# Revit family: CFP - CVP_ISD 1093 Generic
name_source: partatom
category: Windows
revit_build: Autodesk Revit Architecture 2014 (Build: 20130308_1515(x64)
units: mm (PartAtom-declared; Revit-internal decimal feet)

## types (8) — shared parameters
AcousticRating = 37
AllowedRoofSlope = 0°-15°
Analytic Construction = <None>
Assembly Code = B3020110
Coarse Profile = Yes
CoatingInternal = White PVC
Colour = Aluminium profiles / 5 mm toughened glass pane
Count = 1
EmergencyExit = No
Features = Ventilation flat roof window
Finish = PVC Color NCS S 0502-Y
FireRating = E
Function = Flat roof window
Glazing = 5mm Toughened Glass
IsExternal = Yes
LightTransmittance = 0.72
Material = Aluminium profiles / 5 mm toughened glass pane
MaterialsExternal = Aluminium profiles / 5 mm toughened glass pane
Model = Flat roof window
OffsetFromRoof = 400 mm  [stored 1.31234 ft]
Opening Lines Offset = 262.072 mm  [stored 0.859816 ft]
ReactionToFireClass = E
SmokeStop = No
SoundInsulation db = 37
ThermalResistance(R) = 0.0000 (m²·K)/W
UltravioletTransmittance = 0.05
WarrantyYears = 10
ZCEVisible = No
g-value = 0.51
zero-valued in all types: DefaultModel3DSlope, PlacementHeight, ThermalBridge(Installation) W/mK, ZCEHeight

## per-type parameters (varying)
| type | DomeProfileLength | Half Height | HalfHeight | HalfWidth | Height | Height Dome | Height External Profile | Height Outer Glass | Height Top Unit | NominalHeight | NominalWidth | PerimeterWindow m | Thickness Glass | Width | Width External Profile | Width Outer Glass | Width Silk Screen Print | WidthDome | WithinStandardSizes |
| CVP / CFP size 600x600 (060060) | 387.5 mm  [stored 1.27133 ft] | 300 mm  [stored 0.984252 ft] | 387.5 mm  [stored 1.27133 ft] | 387.5 mm  [stored 1.27133 ft] | 780 mm  [stored 2.55906 ft] | 600 mm  [stored 1.9685 ft] | 756 mm  [stored 2.48031 ft] | 746 mm  [stored 2.44751 ft] | 139 mm  [stored 0.456037 ft] | 780 | 780 | 2.4 | 6 mm  [stored 0.019685 ft] | 780 mm  [stored 2.55906 ft] | 756 mm  [stored 2.48031 ft] | 746 mm  [stored 2.44751 ft] | 650 mm  [stored 2.13255 ft] | 600 mm  [stored 1.9685 ft] | Yes |
| CVP / CFP size 1000x1500 (100150) | 587.5 mm | 750 mm  [stored 2.46063 ft] | 837.5 mm  [stored 2.7477 ft] | 587.5 mm | 1680 mm | 1500 mm | 1656 mm | 1646 mm | 190 mm | 1180 | 1680 | 5 | 6 mm  [stored 0.019685 ft] | 1180 mm | 1156 mm  [stored 3.79265 ft] | 1146 mm  [stored 3.75984 ft] | 1050 mm | 1000 mm  [stored 3.28084 ft] | No |
| CVP / CFP size 900x900 (090090) | 537.5 mm | 450 mm  [stored 1.47638 ft] | 537.5 mm | 537.5 mm | 1080 mm  [stored 3.54331 ft] | 900 mm  [stored 2.95276 ft] | 1056 mm  [stored 3.46457 ft] | 1046 mm  [stored 3.43176 ft] | 151 mm  [stored 0.495407 ft] | 1080 | 1080 | 3.6 | 5 mm  [stored 0.0164042 ft] | 1080 mm  [stored 3.54331 ft] | 1056 mm  [stored 3.46457 ft] | 1046 mm  [stored 3.43176 ft] | 950 mm  [stored 3.1168 ft] | 900 mm  [stored 2.95276 ft] | Yes |
| CVP / CFP size 800x800 (080080) | 487.5 mm  [stored 1.59941 ft] | 400 mm  [stored 1.31234 ft] | 487.5 mm  [stored 1.59941 ft] | 487.5 mm  [stored 1.59941 ft] | 980 mm  [stored 3.21522 ft] | 800 mm  [stored 2.62467 ft] | 956 mm  [stored 3.13648 ft] | 946 mm  [stored 3.10367 ft] | 147 mm  [stored 0.482283 ft] | 980 | 980 | 3.2 | 5 mm  [stored 0.0164042 ft] | 980 mm  [stored 3.21522 ft] | 956 mm  [stored 3.13648 ft] | 946 mm  [stored 3.10367 ft] | 850 mm  [stored 2.78871 ft] | 800 mm  [stored 2.62467 ft] | Yes |
| CVP / CFP size 900x1200 (090120) | 537.5 mm | 600 mm  [stored 1.9685 ft] | 687.5 mm  [stored 2.25558 ft] | 537.5 mm | 1380 mm | 1200 mm | 1356 mm | 1346 mm | 169 mm  [stored 0.554462 ft] | 1080 | 1380 | 4.2 | 6 mm  [stored 0.019685 ft] | 1080 mm  [stored 3.54331 ft] | 1056 mm  [stored 3.46457 ft] | 1046 mm  [stored 3.43176 ft] | 950 mm  [stored 3.1168 ft] | 900 mm  [stored 2.95276 ft] | No |
| CVP / CFP size 600x900 (060090) | 387.5 mm  [stored 1.27133 ft] | 450 mm  [stored 1.47638 ft] | 537.5 mm | 387.5 mm  [stored 1.27133 ft] | 1080 mm  [stored 3.54331 ft] | 900 mm  [stored 2.95276 ft] | 1056 mm  [stored 3.46457 ft] | 1046 mm  [stored 3.43176 ft] | 151 mm  [stored 0.495407 ft] | 780 | 1080 | 3 | 5 mm  [stored 0.0164042 ft] | 780 mm  [stored 2.55906 ft] | 756 mm  [stored 2.48031 ft] | 746 mm  [stored 2.44751 ft] | 650 mm  [stored 2.13255 ft] | 600 mm  [stored 1.9685 ft] | No |
| CVP / CFP size 1200x1200 (120120) | 687.5 mm  [stored 2.25558 ft] | 600 mm  [stored 1.9685 ft] | 687.5 mm  [stored 2.25558 ft] | 687.5 mm  [stored 2.25558 ft] | 1380 mm | 1200 mm | 1356 mm | 1346 mm | 169 mm  [stored 0.554462 ft] | 1380 | 1380 | 4.8 | 6 mm  [stored 0.019685 ft] | 1380 mm | 1356 mm | 1346 mm | 1250 mm | 1200 mm | Yes |
| CVP / CFP size 1000x1000 (100100) | 587.5 mm | 500 mm  [stored 1.64042 ft] | 587.5 mm | 587.5 mm | 1180 mm | 1000 mm  [stored 3.28084 ft] | 1156 mm  [stored 3.79265 ft] | 1146 mm  [stored 3.75984 ft] | 156 mm  [stored 0.511811 ft] | 1180 | 1180 | 4 | 5 mm  [stored 0.0164042 ft] | 1180 mm | 1156 mm  [stored 3.79265 ft] | 1146 mm  [stored 3.75984 ft] | 1050 mm | 1000 mm  [stored 3.28084 ft] | Yes |

note: column(s) folded — value = type name in every type: ModelReference, Size

note: [stored X ft] marks values corroborated as IEEE doubles in the binary element streams (Revit-internal decimal feet)
